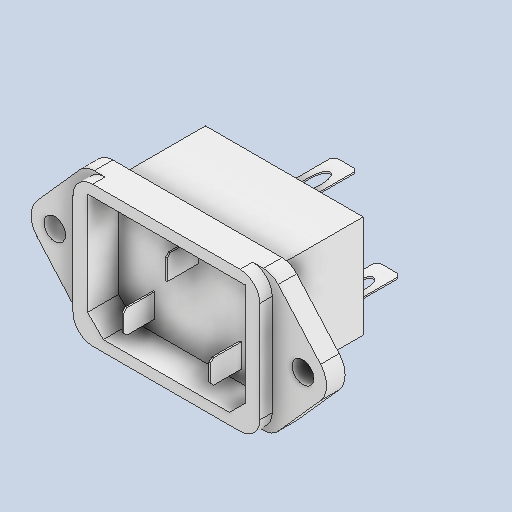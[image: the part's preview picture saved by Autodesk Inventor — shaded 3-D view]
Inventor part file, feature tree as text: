
AUTODESK INVENTOR PART (.ipt)
format: ipt  version: 2022 (Build 260153000, 153)  size: 361,472 bytes
history: native  units: in
note: dims shown in document units (in); Inventor stores cm internally (conversion verified against a paired STEP export)
features: extrude x9, sketch x7, fillet x1, chamfer x1
ambient origin geometry x8: Origin, YZ Plane, XZ Plane, XY Plane, X Axis, Y Axis, Z Axis, Center Point
bodies: Solid1 (feature_tree)
feature tree (18):
  extrude  "Extrusion1"  Depth=0.89in
  extrude  "Extrusion2"  Depth=1.0in
  extrude  "Extrusion3"  TaperAngle=45.0deg  [1 undecoded]
  extrude  "Extrusion4"  TaperAngle=45.0deg  [1 undecoded]
  extrude  "Extrusion5"  Depth=0.0in TaperAngle=0.0deg
  extrude  "Extrusion6"  Depth=0.3in
  extrude  "Extrusion7"  Depth=0.125in
  extrude  "Extrusion8"  Depth=0.125in
  extrude  "Extrusion9"  Depth=0.118in TaperAngle=0.0deg
  fillet  "Fillet1"  Radius=0.197in
  chamfer  "Chamfer1"  Distance=0.551in
  sketch  "Sketch1"  dims[d0=1.185in d1=0.89in]
  sketch  "Sketch2"  dims[d2=0.551in d3=0.0in d4=1.0in]
  sketch  "Sketch4"  dims[d5=0.75in d9=45.0deg]
  sketch  "Sketch5"  dims[d10=0.1in d11=45.0deg]
  sketch  "Sketch6"  dims[d12=0.1in d13=0.0in d14=0.0in]
  sketch  "Sketch7"  dims[d17=0.138in d19=0.3in]
  sketch  "Sketch8"  dims[d20=0.3in d21=0.3067in d24=0.7875in d25=0.118in d26=0.0in d27=0.197in d28=0.0in d29=0.551in d30=0.0in d32=0.075in d36=0.075in d37=0.075in d38=0.075in d39=0.075in d40=0.1in d41=0.06in d42=1.0063in d43=0.06in d44=0.075in d45=0.06in d46=0.075in d47=0.06in d48=0.075in d49=0.1in d50=0.075in d51=0.06in d52=0.005in d53=0.0in d54=0.01in d55=0.01in d56=0.01in d57=0.384in d58=0.0in d59=0.097in d60=0.039in d61=0.097in d62=0.097in d63=0.039in d64=0.039in d65=0.075in d66=0.075in d67=0.075in d68=0.1945in d69=0.1945in d70=0.0in d71=0.0in d75=0.01in d79=90.0deg d80=0.15in d81=0.01in d82=0.15in d83=0.01in d84=0.005in d89=0.01in d90=0.15in d91=0.01in d92=0.005in d93=0.07in d94=0.197in d95=0.0in d96=0.125in d97=0.02in d98=0.125in d99=45.0deg]
note: 2 required parameter values undecoded (feature->parameter linkage not recoverable at this tier; creation-order binding heuristic only, values carry confidence <= 0.55)
